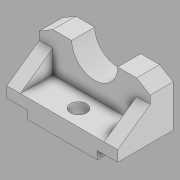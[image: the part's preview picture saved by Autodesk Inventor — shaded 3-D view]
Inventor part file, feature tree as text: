
AUTODESK INVENTOR PART (.ipt)
format: ipt  version: 2020 (Build 240168000, 168)  size: 185,344 bytes
history: native  units: mm
features: extrude x10, sketch x10, other x1
ambient origin geometry x8: Origin, YZ Plane, XZ Plane, XY Plane, X Axis, Y Axis, Z Axis, Center Point
bodies: Body1 (feature_tree)
feature tree (21):
  other  "Sólido1"
  extrude  "Base"  Depth=86.0mm
  extrude  "Orificio_Inferior_Derecho"  Depth=30.0mm
  extrude  "Orificio_Inferior_Izquierdo"  Depth=82.0mm TaperAngle=0.0deg
  extrude  "Medio_Círculo"  Depth=12.0mm
  extrude  "Hueco"  Depth=82.0mm
  extrude  "Círculo"  TaperAngle=0.0deg  [1 undecoded]
  extrude  "Triángulo_Derecho"  Depth=28.0mm
  extrude  "Triángulo_Izquierdo"  Depth=82.0mm
  extrude  "Recorte_Superior_Derecho"  Depth=24.0mm
  extrude  "Recorte_Superior_Izquierdo"  Depth=34.0mm
  sketch  "Boceto1"  dims[d0=164.0mm d1=86.0mm]
  sketch  "Boceto2"  dims[d2=82.0mm d3=0.0mm d4=30.0mm]
  sketch  "Boceto3"  dims[d5=12.0mm d6=82.0mm d7=0.0mm]
  sketch  "Boceto5"  dims[d8=30.0mm d9=12.0mm]
  sketch  "Boceto7"  dims[d10=82.0mm d11=0.0mm d15=68.0mm]
  sketch  "Boceto8"  dims[d16=34.0mm d17=0.0mm d23=0.0mm]
  sketch  "Boceto9"  dims[d24=0.0mm d25=28.0mm]
  sketch  "Boceto10"  dims[d26=48.0mm d27=0.0mm d28=82.0mm]
  sketch  "Boceto11"  dims[d29=24.0mm d30=24.0mm]
  sketch  "Boceto12"  dims[d31=28.0mm d32=0.0mm d33=34.0mm d34=20.0mm d35=0.0mm d36=34.0mm d37=20.0mm d38=0.0mm d39=20.0mm d40=62.0mm d41=24.0mm d42=12.0mm d43=34.0mm d44=0.0mm d45=12.0mm d46=20.0mm d47=34.0mm d48=0.0mm d18=0.872665mm]
note: 1 required parameter value undecoded (feature->parameter linkage not recoverable at this tier; creation-order binding heuristic only, values carry confidence <= 0.55)
